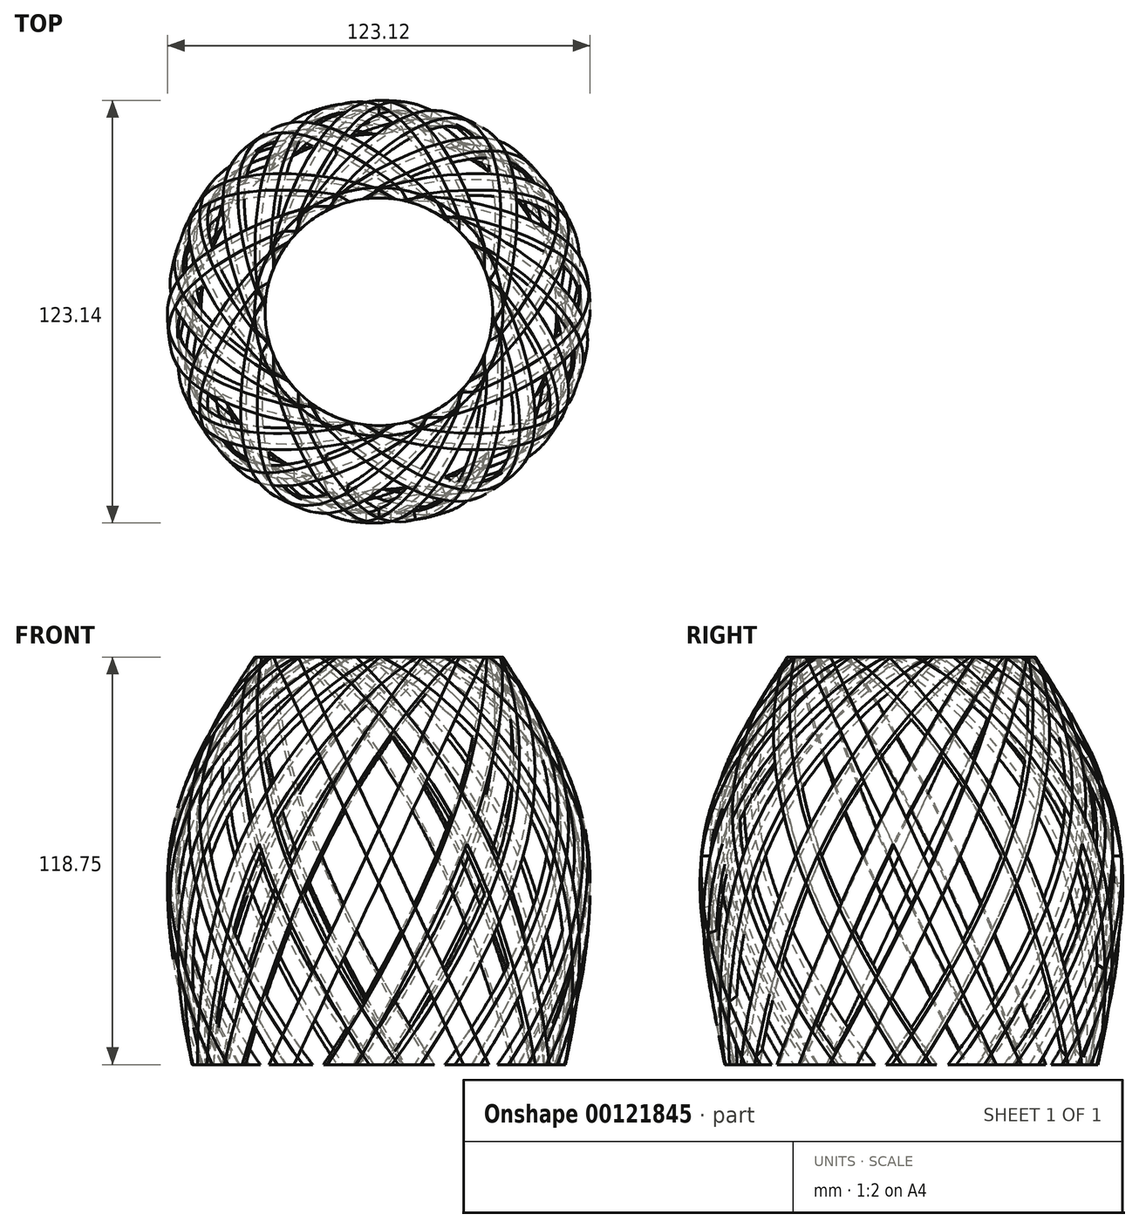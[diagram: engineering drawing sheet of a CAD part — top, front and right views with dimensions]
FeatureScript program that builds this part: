
annotation { "Feature Type Name" : "Feature", "Feature Type Description" : "" }
export const myFeature = defineFeature(function(context is Context, id is Id, definition is map)
    precondition{}
    {
        {
            var Q0;
            Q0=qCreatedBy(makeId("Front.planeOp"),FACE);
            var sketch = newSketch(context, id + "F0", { "sketchPlane" : qUnion([Q0])});
            skLineSegment(sketch, "E0", {"start": v(0, -58.24) * mm, "end": v(0, 60.51) * mm});
            skLineSegment(sketch, "E1", {"start": v(0, 60.51) * mm, "end": v(-36.17, 60.51) * mm});
            skLineSegment(sketch, "E2", {"start": v(0, -58.24) * mm, "end": v(-54.37, -58.24) * mm});
            skFitSpline(sketch, "E3", {"points": [v(-54.37, -58.24) * mm, v(-60.29, 9.1) * mm, v(-36.17, 60.51) * mm], "startDerivative": vector(-27.45, 134.68) * mm, "endDerivative": vector(65.2, 102.36) * mm});
            skSolve(sketch);
        }
        {
            var Q0;
            Q0=makeQuery(id+"F0.imprint","IMPRINT",FACE,{"disambiguationData":[TD([[makeQuery(id+"F0.imprint","IMPRINT",EDGE,{"derivedFrom":sQuery(id+"F0.wireOp",EDGE,"E0")}),1.0]])]});
            var Q1;
            Q1=sQuery(id+"F0.wireOp",EDGE,"E0");
            revolve(context, id + "F1", {"entities" : qUnion([Q0]), "axis" : qUnion([Q1]), "revolveType" : RevolveType.FULL});
        }
        {
            var Q0;
            Q0=makeQuery(id+"F1.opRevolve","SWEPT_FACE",FACE,{"disambiguationData":[OSD([sQuery(id+"F0.wireOp",EDGE,"E1")])]});
            var Q1;
            Q1=makeQuery(id+"F1.opRevolve","SWEPT_FACE",FACE,{"disambiguationData":[OSD([sQuery(id+"F0.wireOp",EDGE,"E2")])]});
            shell(context, id + "F2", {"entities" : qUnion([Q0, Q1]), "thickness" : 2.54 * mm});
        }
        {
            var Q0;
            Q0=qCreatedBy(makeId("Front.planeOp"),FACE);
            var sketch = newSketch(context, id + "F3", { "sketchPlane" : qUnion([Q0])});
            skLineSegment(sketch, "E4.0", {"start": v(0, 60.51) * mm, "end": v(-36.17, 60.51) * mm});
            skFitSpline(sketch, "E5.0", {"points": [v(-54.37, -58.24) * mm, v(-59.15, -34.82) * mm, v(-68.3, 10.08) * mm, v(-46.56, 44.2) * mm, v(-36.17, 60.51) * mm]});
            skLineSegment(sketch, "E6.0", {"start": v(0, -58.24) * mm, "end": v(-54.37, -58.24) * mm});
            skLineSegment(sketch, "E7.0", {"start": v(54.37, -58.24) * mm, "end": v(-54.37, -58.24) * mm});
            skLineSegment(sketch, "E8.0", {"start": v(36.17, 60.51) * mm, "end": v(-36.17, 60.51) * mm});
            skFitSpline(sketch, "E9.MirrorCS", {"points": [v(54.37, -58.24) * mm, v(59.15, -34.82) * mm, v(68.3, 10.08) * mm, v(46.56, 44.2) * mm, v(36.17, 60.51) * mm]});
            skLineSegment(sketch, "E10", {"start": v(-30.73, 60.51) * mm, "end": v(24.72, -58.24) * mm});
            skLineSegment(sketch, "E11", {"start": v(-23.46, 60.51) * mm, "end": v(32, -58.24) * mm});
            skSolve(sketch);
        }
        {
            var Q0;
            {var subQ0=sQuery(id+"F3.wireOp",EDGE,"E10");Q0=makeQuery(id+"F3.imprint","IMPRINT",FACE,{"disambiguationData":[TD([[makeQuery(id+"F3.imprint","IMPRINT",EDGE,{"derivedFrom":subQ0}),1.0]])]});}
            extrude(context, id + "F4", {"entities" : qUnion([Q0]), "operationType" : NewBodyOperationType.INTERSECT, "endBound" : BoundingType.SYMMETRIC, "depth" : 200 * mm});
        }
        {
            var Q0;
            Q0=makeQuery(id+"F4.boolean.opBoolean","SPLIT",BODY,{"disambiguationData":[OD(0.0)],"derivedFrom":makeQuery(id+"F1.opRevolve","SWEPT_BODY",BODY,{"disambiguationData":[OSD([sQuery(id+"F0.wireOp",EDGE,"E0"),sQuery(id+"F0.wireOp",EDGE,"E1"),sQuery(id+"F0.wireOp",EDGE,"E2"),sQuery(id+"F0.wireOp",EDGE,"E3")])]})});
            var Q1;
            Q1=sQuery(id+"F0.wireOp",EDGE,"E0");
            circularPattern(context, id + "F5", {"entities" : qUnion([Q0]), "axis" : qUnion([Q1]), "angle" : 20 * degree, "instanceCount" : 20});
        }
        {
            var Q0;
            Q0=makeQuery(id+"F4.boolean.opBoolean","SPLIT",BODY,{"disambiguationData":[OD(1.0)],"derivedFrom":makeQuery(id+"F1.opRevolve","SWEPT_BODY",BODY,{"disambiguationData":[OSD([sQuery(id+"F0.wireOp",EDGE,"E0"),sQuery(id+"F0.wireOp",EDGE,"E1"),sQuery(id+"F0.wireOp",EDGE,"E2"),sQuery(id+"F0.wireOp",EDGE,"E3")])]})});
            var Q1;
            Q1=sQuery(id+"F0.wireOp",EDGE,"E0");
            circularPattern(context, id + "F6", {"entities" : qUnion([Q0]), "axis" : qUnion([Q1]), "angle" : 30 * degree, "instanceCount" : 20});
        }
    });
